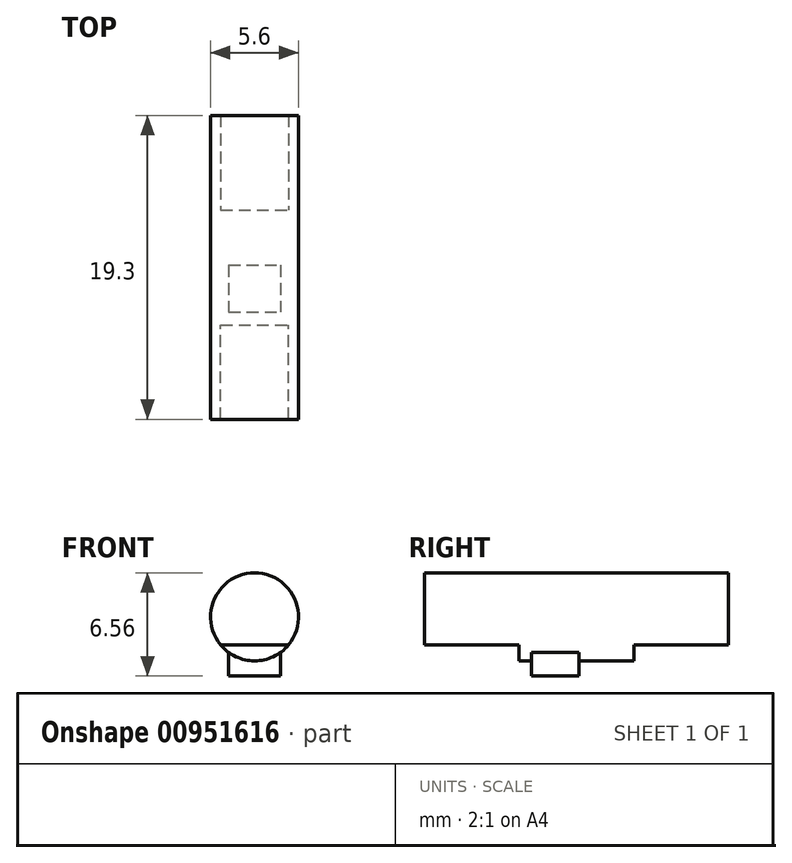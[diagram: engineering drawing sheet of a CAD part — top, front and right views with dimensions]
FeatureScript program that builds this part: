
annotation { "Feature Type Name" : "Feature", "Feature Type Description" : "" }
export const myFeature = defineFeature(function(context is Context, id is Id, definition is map)
    precondition{}
    {
        {
            var Q0;
            Q0=qCreatedBy(makeId("Front.planeOp"),FACE);
            var sketch = newSketch(context, id + "F0", { "sketchPlane" : qUnion([Q0])});
            skCircle(sketch, "E0", {"center": v(0, 0) * mm, "radius": 2.8 * mm});
            skPoint(sketch, "E1", {"position": v(-2.15, -1.79) * mm});
            skPoint(sketch, "E2", {"position": v(2.15, -1.79) * mm});
            skLineSegment(sketch, "E3", {"start": v(-2.15, -1.79) * mm, "end": v(2.15, -1.79) * mm});
            skSolve(sketch);
        }
        {
            assignVariable(context, id + "F1", {"name" : "Shaft_Length", "anyValue" : 1.3});
        }
        {
            var Q0;
            {var subQ0=sQuery(id+"F0.wireOp",EDGE,"E3");Q0=makeQuery(id+"F0.imprint","IMPRINT",FACE,{"disambiguationData":[TD([[makeQuery(id+"F0.imprint","IMPRINT",EDGE,{"derivedFrom":subQ0}),1.0]])]});}
            extrude(context, id + "F2", {"entities" : qUnion([Q0]), "depth" : 6 * mm, "offsetDistance" : 25 * mm});
        }
        {
            var Q0;
            Q0=qSketchRegion(id+"F0",true);
            extrude(context, id + "F3", {"entities" : qUnion([Q0]), "operationType" : NewBodyOperationType.ADD, "oppositeDirection" : true, "depth" : (getVariable(context, 'Shaft_Length') - 0.5) * mm, "offsetDistance" : 25 * mm});
        }
        {
            var Q0;
            Q0=makeQuery(id+"F3.opExtrude","CAP_FACE",FACE,{"disambiguationData":[OSD([sQuery(id+"F0.wireOp",EDGE,"E0")])],"isStart":false});
            var sketch = newSketch(context, id + "F4", { "sketchPlane" : qUnion([Q0])});
            skPoint(sketch, "E4", {"position": v(-1.65, 2.26) * mm});
            skPoint(sketch, "E5", {"position": v(1.65, 2.26) * mm});
            skLineSegment(sketch, "E6", {"start": v(1.65, -2.26) * mm, "end": v(1.65, -3.76) * mm});
            skLineSegment(sketch, "E7.MirrorCS", {"start": v(-1.65, -2.26) * mm, "end": v(-1.65, -3.76) * mm});
            skLineSegment(sketch, "E8", {"start": v(1.65, -3.76) * mm, "end": v(-1.65, -3.76) * mm});
            skArc(sketch, "E9", {"start": v(1.65, -2.26) * mm, "mid": v(0, 2.8) * mm, "end": v(-1.65, -2.26) * mm});
            skSolve(sketch);
        }
        {
            var Q0;
            Q0=qSketchRegion(id+"F4",true);
            extrude(context, id + "F5", {"entities" : qUnion([Q0]), "operationType" : NewBodyOperationType.ADD, "depth" : 3 * mm, "offsetDistance" : 25 * mm});
        }
        {
            var Q0;
            Q0=makeQuery(id+"F5.opExtrude","CAP_FACE",FACE,{"disambiguationData":[OSD([sQuery(id+"F4.wireOp",EDGE,"E6"),sQuery(id+"F4.wireOp",EDGE,"E7.MirrorCS"),sQuery(id+"F4.wireOp",EDGE,"E8"),sQuery(id+"F4.wireOp",EDGE,"E9")])],"isStart":false});
            var sketch = newSketch(context, id + "F6", { "sketchPlane" : qUnion([Q0])});
            skCircle(sketch, "E10.0", {"center": v(0, 0) * mm, "radius": 2.8 * mm});
            skPoint(sketch, "E10.1", {"position": v(2.15, -1.79) * mm});
            skPoint(sketch, "E10.2", {"position": v(-2.15, -1.79) * mm});
            skSolve(sketch);
        }
        {
            var Q0;
            Q0=qSketchRegion(id+"F6",true);
            extrude(context, id + "F7", {"entities" : qUnion([Q0]), "operationType" : NewBodyOperationType.ADD, "depth" : 3.5 * mm, "offsetDistance" : 25 * mm});
        }
        {
            var Q0;
            Q0=makeQuery(id+"F7.opExtrude","CAP_FACE",FACE,{"disambiguationData":[OSD([sQuery(id+"F6.wireOp",EDGE,"E10.0")])],"isStart":false});
            var sketch = newSketch(context, id + "F8", { "sketchPlane" : qUnion([Q0])});
            skArc(sketch, "E11.0.0", {"start": v(-2.15, -1.79) * mm, "mid": v(0, 2.8) * mm, "end": v(2.15, -1.79) * mm});
            skLineSegment(sketch, "E11.0.1", {"start": v(2.15, -1.79) * mm, "end": v(-2.15, -1.79) * mm});
            skSolve(sketch);
        }
        {
            var Q0;
            Q0=qSketchRegion(id+"F8",true);
            extrude(context, id + "F9", {"entities" : qUnion([Q0]), "operationType" : NewBodyOperationType.ADD, "depth" : 6 * mm, "offsetDistance" : 25 * mm});
        }
    });
